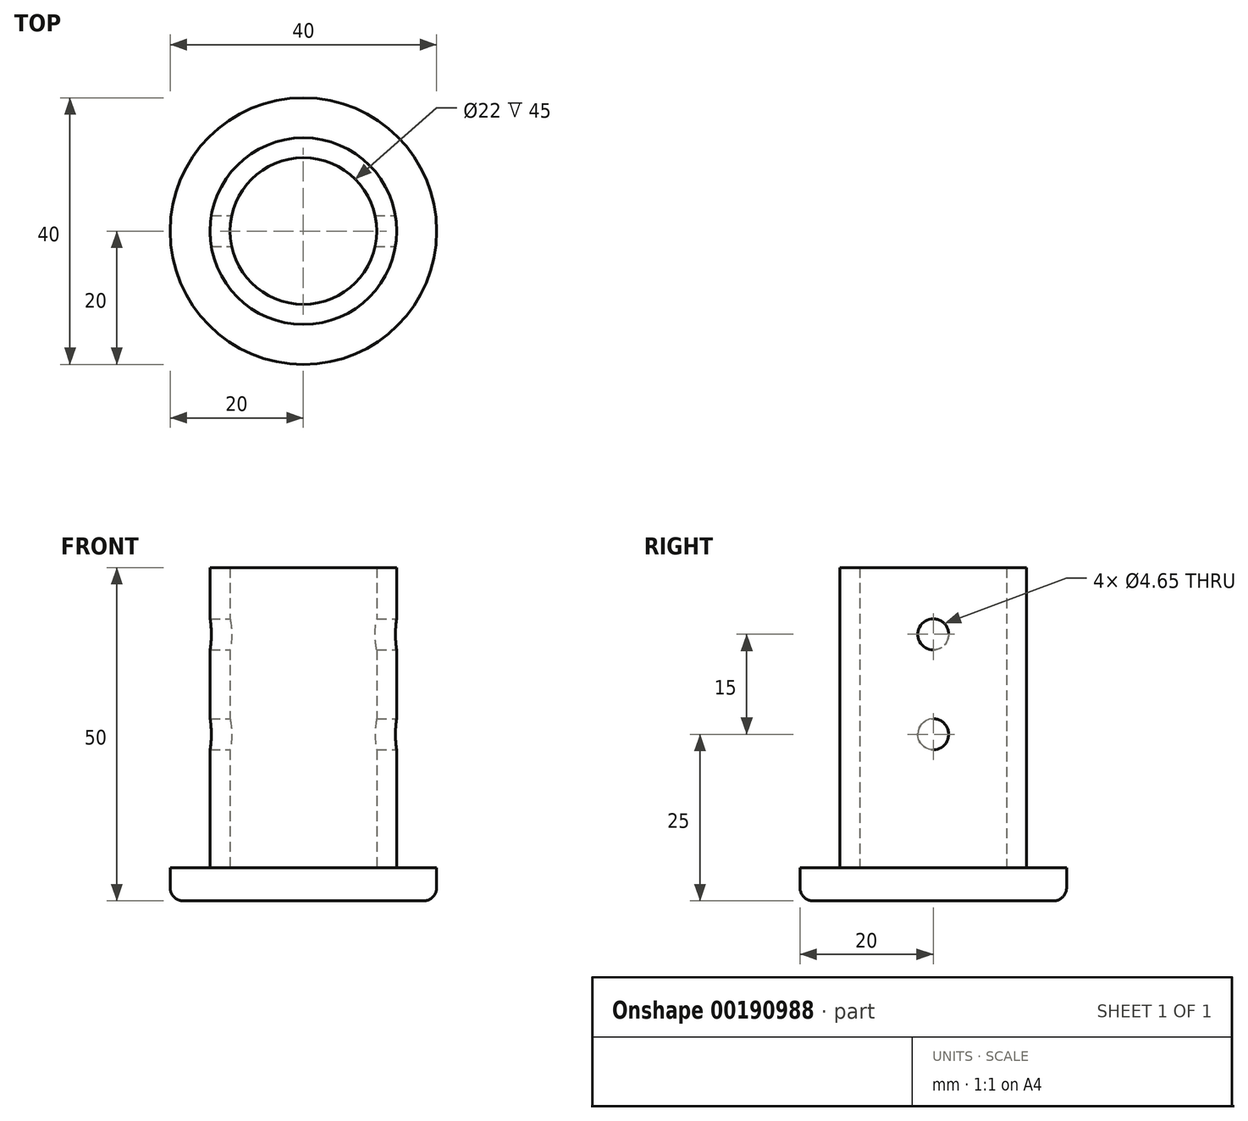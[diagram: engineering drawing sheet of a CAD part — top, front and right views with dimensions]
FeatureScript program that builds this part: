
annotation { "Feature Type Name" : "Feature", "Feature Type Description" : "" }
export const myFeature = defineFeature(function(context is Context, id is Id, definition is map)
    precondition{}
    {
        {
            var Q0;
            Q0=qCreatedBy(makeId("Top.planeOp"),FACE);
            var sketch = newSketch(context, id + "F0", { "sketchPlane" : qUnion([Q0])});
            skCircle(sketch, "E0", {"center": v(0, 0) * mm, "radius": 14 * mm});
            skCircle(sketch, "E1", {"center": v(0, 0) * mm, "radius": 20 * mm});
            skCircle(sketch, "E2.0", {"center": v(0, 0) * mm, "radius": 11 * mm});
            skCircle(sketch, "E3", {"center": v(34.73, 0) * mm, "radius": 2.25 * mm});
            skCircle(sketch, "E4", {"center": v(-31.63, 0) * mm, "radius": 2.25 * mm});
            skCircle(sketch, "E5", {"center": v(34.73, 0) * mm, "radius": 4.5 * mm});
            skCircle(sketch, "E6", {"center": v(-31.63, 0) * mm, "radius": 4.5 * mm});
            skSolve(sketch);
        }
        {
            var Q0;
            Q0=makeQuery(id+"F0.imprint","IMPRINT",FACE,{"disambiguationData":[TD([[makeQuery(id+"F0.imprint","IMPRINT",EDGE,{"derivedFrom":sQuery(id+"F0.wireOp",EDGE,"E0")}),1.0]])]});
            extrude(context, id + "F1", {"entities" : qUnion([Q0]), "depth" : 50 * mm});
        }
        {
            var Q0;
            Q0=makeQuery(id+"F0.imprint","IMPRINT",FACE,{"disambiguationData":[TD([[makeQuery(id+"F0.imprint","IMPRINT",EDGE,{"derivedFrom":sQuery(id+"F0.wireOp",EDGE,"E0")}),-1.0]])]});
            var Q1;
            Q1=makeQuery(id+"F0.imprint","IMPRINT",FACE,{"disambiguationData":[TD([[makeQuery(id+"F0.imprint","IMPRINT",EDGE,{"derivedFrom":sQuery(id+"F0.wireOp",EDGE,"E0")}),-1.0]])]});
            extrude(context, id + "F2", {"entities" : qUnion([Q0, Q1]), "operationType" : NewBodyOperationType.ADD, "depth" : 5 * mm});
        }
        {
            var Q0;
            Q0=makeQuery(id+"F0.imprint","IMPRINT",FACE,{"disambiguationData":[TD([[makeQuery(id+"F0.imprint","IMPRINT",EDGE,{"derivedFrom":sQuery(id+"F0.wireOp",EDGE,"E2.0")}),1.0]])]});
            extrude(context, id + "F3", {"entities" : qUnion([Q0]), "operationType" : NewBodyOperationType.ADD, "depth" : 5 * mm});
        }
        {
            var Q0;
            Q0=makeQuery(id+"F2.opExtrude","CAP_EDGE",EDGE,{"disambiguationData":[OSD([sQuery(id+"F0.wireOp",EDGE,"E1")])],"isStart":true});
            fillet(context, id + "F4", {"entities" : qUnion([Q0]), "radius" : 2 * mm, "tangentPropagation" : true, "allowEdgeOverflow" : false});
        }
        {
            var Q0;
            Q0=qCreatedBy(makeId("Right.planeOp"),FACE);
            var sketch = newSketch(context, id + "F5", { "sketchPlane" : qUnion([Q0])});
            skLineSegment(sketch, "E7", {"start": v(0, 0) * mm, "end": v(0, 25) * mm});
            skLineSegment(sketch, "E8", {"start": v(0, 25) * mm, "end": v(0, 40) * mm});
            skCircle(sketch, "E9", {"center": v(0, 25) * mm, "radius": 2.33 * mm});
            skCircle(sketch, "E10", {"center": v(0, 40) * mm, "radius": 2.33 * mm});
            skSolve(sketch);
        }
        {
            var Q0;
            Q0=makeQuery(id+"F5.imprint","IMPRINT",FACE,{"disambiguationData":[TD([[makeQuery(id+"F5.imprint","IMPRINT",EDGE,{"derivedFrom":sQuery(id+"F5.wireOp",EDGE,"E10")}),1.0]])]});
            var Q1;
            {var subQ0=sQuery(id+"F5.wireOp",EDGE,"E8");var subQ1=sQuery(id+"F5.wireOp",EDGE,"E7");var subQ2=makeQuery(id+"F5.imprint","INTERSECT",VERTEX,{"derivedFrom":[subQ1,subQ0]});Q1=makeQuery(id+"F5.imprint","IMPRINT",FACE,{"disambiguationData":[TD([[makeQuery(id+"F5.imprint","IMPRINT",EDGE,{"disambiguationData":[TD([[subQ2,1.0]])],"derivedFrom":subQ1}),-1.0]])]});}
            var Q2;
            {var subQ0=sQuery(id+"F5.wireOp",EDGE,"E8");var subQ1=sQuery(id+"F5.wireOp",EDGE,"E7");var subQ2=makeQuery(id+"F5.imprint","INTERSECT",VERTEX,{"derivedFrom":[subQ1,subQ0]});Q2=makeQuery(id+"F5.imprint","IMPRINT",FACE,{"disambiguationData":[TD([[makeQuery(id+"F5.imprint","IMPRINT",EDGE,{"disambiguationData":[TD([[subQ2,1.0]])],"derivedFrom":subQ1}),1.0]])]});}
            var Q3;
            Q3=sQuery(id+"F5.wireOp",EDGE,"E9");
            var Q4;
            Q4=sQuery(id+"F5.wireOp",EDGE,"E10");
            extrude(context, id + "F6", {"entities" : qUnion([Q0, Q1, Q2]), "operationType" : NewBodyOperationType.REMOVE, "surfaceEntities" : qUnion([Q3, Q4]), "endBound" : BoundingType.THROUGH_ALL, "oppositeDirection" : true, "depth" : 25 * mm, "hasSecondDirection" : true, "secondDirectionOppositeDirection" : false, "secondDirectionDepth" : 25 * mm});
        }
    });
